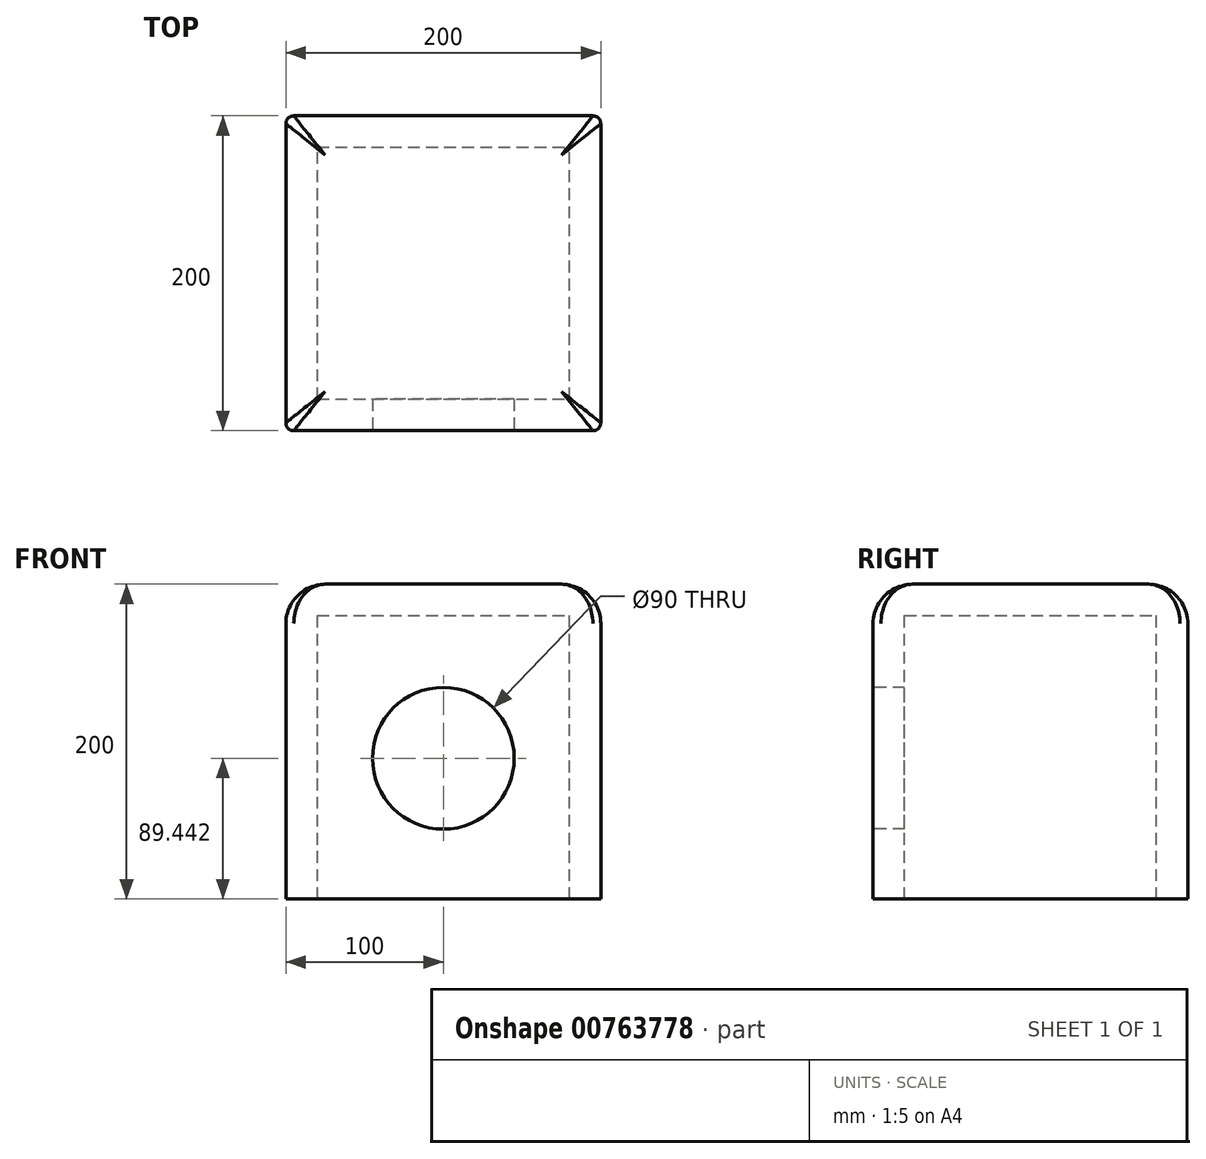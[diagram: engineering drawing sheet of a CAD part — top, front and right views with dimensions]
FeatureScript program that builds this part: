
annotation { "Feature Type Name" : "Feature", "Feature Type Description" : "" }
export const myFeature = defineFeature(function(context is Context, id is Id, definition is map)
    precondition{}
    {
        {
            var Q0;
            Q0=qCreatedBy(makeId("Front.planeOp"),FACE);
            var sketch = newSketch(context, id + "F0", { "sketchPlane" : qUnion([Q0])});
            skLineSegment(sketch, "E0.bottom", {"start": v(0, 0) * mm, "end": v(200, 0) * mm});
            skLineSegment(sketch, "E0.top", {"start": v(0, 200) * mm, "end": v(200, 200) * mm});
            skLineSegment(sketch, "E0.left", {"start": v(0, 0) * mm, "end": v(0, 200) * mm});
            skLineSegment(sketch, "E0.right", {"start": v(200, 0) * mm, "end": v(200, 200) * mm});
            skSolve(sketch);
        }
        {
            var Q0;
            Q0=makeQuery(id+"F0.imprint","IMPRINT",FACE,{"disambiguationData":[TD([[makeQuery(id+"F0.imprint","IMPRINT",EDGE,{"derivedFrom":sQuery(id+"F0.wireOp",EDGE,"E0.bottom")}),1.0]])]});
            extrude(context, id + "F1", {"entities" : qUnion([Q0]), "depth" : 200 * mm, "offsetDistance" : 25 * mm});
        }
        {
            var Q0;
            Q0=makeQuery(id+"F1.opExtrude","CAP_FACE",FACE,{"disambiguationData":[OSD([sQuery(id+"F0.wireOp",EDGE,"E0.bottom"),sQuery(id+"F0.wireOp",EDGE,"E0.top"),sQuery(id+"F0.wireOp",EDGE,"E0.left"),sQuery(id+"F0.wireOp",EDGE,"E0.right")])],"isStart":false});
            var sketch = newSketch(context, id + "F2", { "sketchPlane" : qUnion([Q0])});
            skCircle(sketch, "E1", {"center": v(100, 89.44) * mm, "radius": 45 * mm});
            skPoint(sketch, "E1.centerSnap0", {"position": v(100, 0) * mm});
            skSolve(sketch);
        }
        {
            var Q0;
            Q0=makeQuery(id+"F1.opExtrude","SWEPT_FACE",FACE,{"disambiguationData":[OSD([sQuery(id+"F0.wireOp",EDGE,"E0.bottom")])]});
            shell(context, id + "F3", {"entities" : qUnion([Q0]), "thickness" : 20 * mm});
        }
        {
            var Q0;
            Q0=makeQuery(id+"F2.imprint","IMPRINT",FACE,{"disambiguationData":[TD([[makeQuery(id+"F2.imprint","IMPRINT",EDGE,{"derivedFrom":sQuery(id+"F2.wireOp",EDGE,"E1")}),1.0]])]});
            var Q1;
            Q1=sQuery(id+"F2.wireOp",EDGE,"E1");
            extrude(context, id + "F4", {"entities" : qUnion([Q0]), "operationType" : NewBodyOperationType.REMOVE, "surfaceEntities" : qUnion([Q1]), "oppositeDirection" : true, "depth" : 57 * mm, "offsetDistance" : 25 * mm});
        }
        {
            var Q0;
            Q0=makeQuery(id+"F1.opExtrude","CAP_EDGE",EDGE,{"disambiguationData":[OSD([sQuery(id+"F0.wireOp",EDGE,"E0.top")])],"isStart":false});
            var Q1;
            Q1=makeQuery(id+"F1.opExtrude","SWEPT_EDGE",EDGE,{"disambiguationData":[OSD([sQuery(id+"F0.wireOp",EDGE,"E0.top"),sQuery(id+"F0.wireOp",EDGE,"E0.left")])]});
            var Q2;
            Q2=makeQuery(id+"F1.opExtrude","CAP_EDGE",EDGE,{"disambiguationData":[OSD([sQuery(id+"F0.wireOp",EDGE,"E0.top")])],"isStart":true});
            var Q3;
            Q3=makeQuery(id+"F1.opExtrude","SWEPT_EDGE",EDGE,{"disambiguationData":[OSD([sQuery(id+"F0.wireOp",EDGE,"E0.top"),sQuery(id+"F0.wireOp",EDGE,"E0.right")])]});
            fillet(context, id + "F5", {"entities" : qUnion([Q0, Q1, Q2, Q3]), "radius" : 25 * mm, "tangentPropagation" : true, "allowEdgeOverflow" : false});
        }
        {
            var Q0;
            Q0=makeQuery(id+"F1.opExtrude","CAP_EDGE",EDGE,{"disambiguationData":[OSD([sQuery(id+"F0.wireOp",EDGE,"E0.left")])],"isStart":false});
            var Q1;
            Q1=makeQuery(id+"F1.opExtrude","CAP_EDGE",EDGE,{"disambiguationData":[OSD([sQuery(id+"F0.wireOp",EDGE,"E0.right")])],"isStart":false});
            var Q2;
            Q2=makeQuery(id+"F1.opExtrude","CAP_EDGE",EDGE,{"disambiguationData":[OSD([sQuery(id+"F0.wireOp",EDGE,"E0.left")])],"isStart":true});
            var Q3;
            Q3=makeQuery(id+"F1.opExtrude","CAP_EDGE",EDGE,{"disambiguationData":[OSD([sQuery(id+"F0.wireOp",EDGE,"E0.right")])],"isStart":true});
            fillet(context, id + "F6", {"entities" : qUnion([Q0, Q1, Q2, Q3]), "radius" : 5 * mm, "tangentPropagation" : true, "allowEdgeOverflow" : false});
        }
    });
